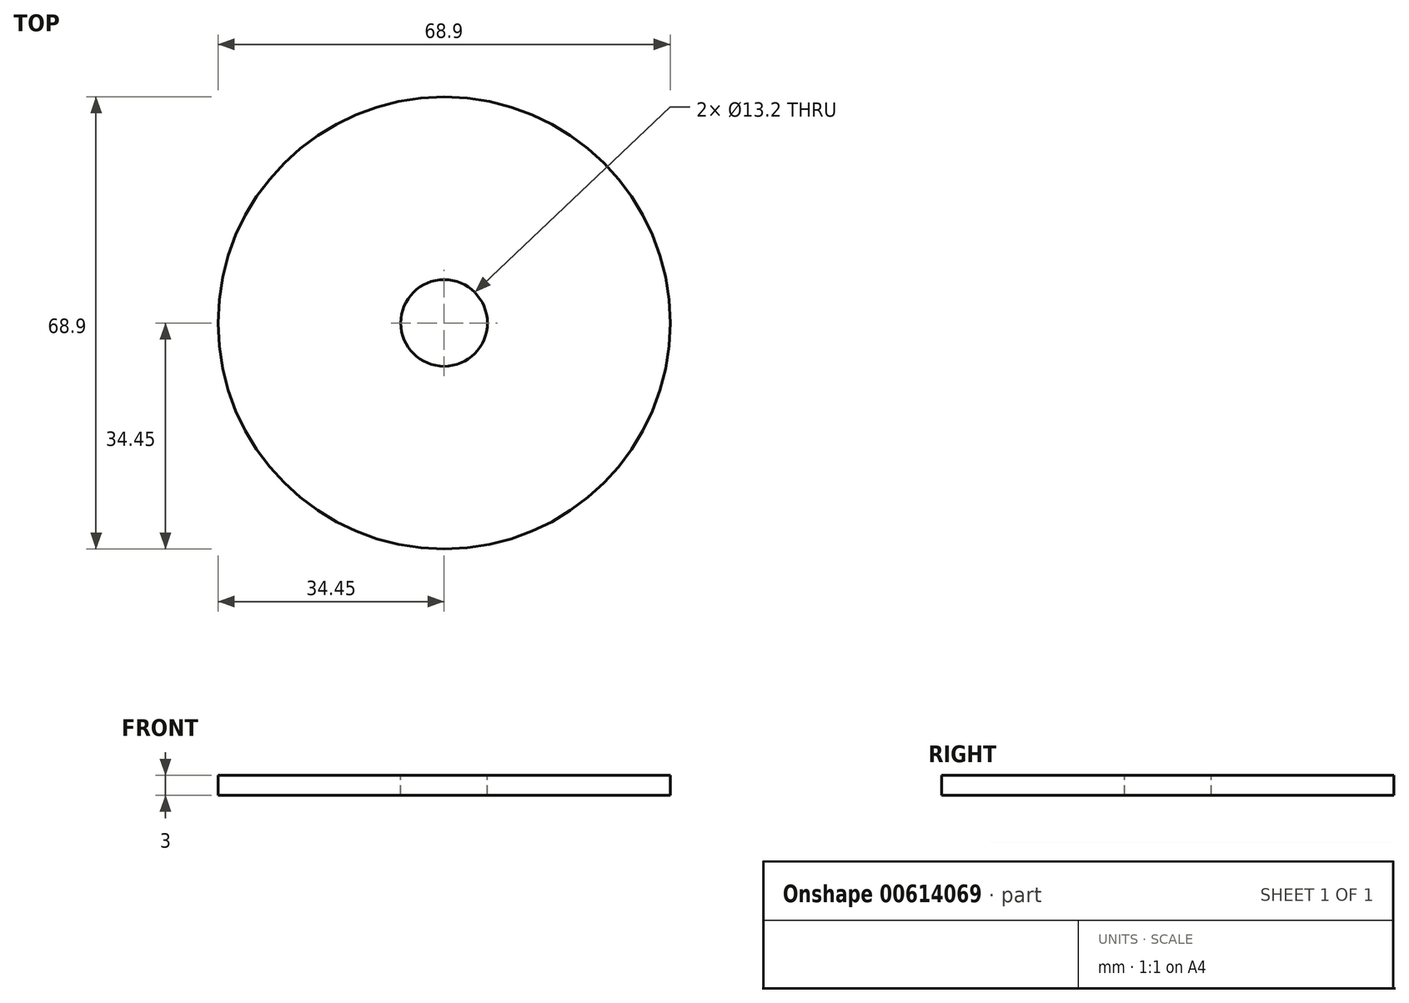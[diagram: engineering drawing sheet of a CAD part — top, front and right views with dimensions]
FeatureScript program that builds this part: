
annotation { "Feature Type Name" : "Feature", "Feature Type Description" : "" }
export const myFeature = defineFeature(function(context is Context, id is Id, definition is map)
    precondition{}
    {
        {
            var Q0;
            Q0=qCreatedBy(makeId("Top.planeOp"),FACE);
            var sketch = newSketch(context, id + "F0", { "sketchPlane" : qUnion([Q0])});
            skCircle(sketch, "E0", {"center": v(0, 0) * mm, "radius": 34.45 * mm});
            skSolve(sketch);
        }
        {
            var Q0;
            Q0=makeQuery(id+"F0.imprint","IMPRINT",FACE,{"disambiguationData":[TD([[makeQuery(id+"F0.imprint","IMPRINT",EDGE,{"derivedFrom":sQuery(id+"F0.wireOp",EDGE,"E0")}),1.0]])]});
            var Q1;
            Q1=qSketchRegion(id+"FGpqzCAi0RanXPu_0",true);
            extrude(context, id + "F1", {"entities" : qUnion([Q0, Q1]), "oppositeDirection" : true, "depth" : 3 * mm, "offsetDistance" : 25 * mm});
        }
        {
            var Q0;
            Q0=qCreatedBy(makeId("Top.planeOp"),FACE);
            var sketch = newSketch(context, id + "F2", { "sketchPlane" : qUnion([Q0])});
            skPoint(sketch, "E1", {"position": v(0, 0) * mm});
            skSolve(sketch);
        }
        {
            var Q0;
            Q0=sQuery(id+"F2.wireOp",VERTEX,"E1");
            var Q1;
            Q1=makeQuery(id+"F1.opExtrude","SWEPT_BODY",BODY,{"disambiguationData":[OSD([sQuery(id+"F0.wireOp",EDGE,"E0")])]});
            hole(context, id + "F3", {"style" : HoleStyle.SIMPLE, "endStyle" : HoleEndStyle.THROUGH, "standardTappedOrClearance" : lookupTablePath({ "standard" : "ISO", "fit" : "Normal", "size" : "M12", "type" : "Clearance" }), "standardBlindInLast" : lookupTablePath({ "fit" : "Standard", "standard" : "ISO", "size" : "M12", "type" : "Clearance" }), "holeDiameter" : 13.2 * mm, "majorDiameter" : 5 * mm, "isTappedThrough" : true, "tappedDepth" : 12 * mm, "tapClearance" : 3, "locations" : qUnion([Q0]), "scope" : qUnion([Q1])});
        }
        {
            var Q0;
            Q0=makeQuery(id+"F1.opExtrude","SWEPT_BODY",BODY,{"disambiguationData":[OSD([sQuery(id+"F0.wireOp",EDGE,"E0")])]});
            transform(context, id + "F4", {"entities" : qUnion([Q0]), "transformType" : TransformType.TRANSLATION_3D, "dx" : 0 * mm, "dy" : 0 * mm, "dz" : 0 * mm, "makeCopy" : true});
        }
        {
            var Q0;
            Q0=makeQuery(id+"F4.opPattern","COPY",BODY,{"derivedFrom":makeQuery(id+"F1.opExtrude","SWEPT_BODY",BODY,{"disambiguationData":[OSD([sQuery(id+"F0.wireOp",EDGE,"E0")])]}),"instanceName":"1"});
            deleteBodies(context, id + "F5", {"entities" : qUnion([Q0])});
        }
        {
            var Q0;
            Q0=makeQuery(id+"F1.opExtrude","SWEPT_BODY",BODY,{"disambiguationData":[OSD([sQuery(id+"F0.wireOp",EDGE,"E0")])]});
            transform(context, id + "F6", {"entities" : qUnion([Q0]), "transformType" : TransformType.TRANSLATION_3D, "dx" : 0 * mm, "dy" : 0 * mm, "dz" : 0 * mm, "makeCopy" : true});
        }
    });
